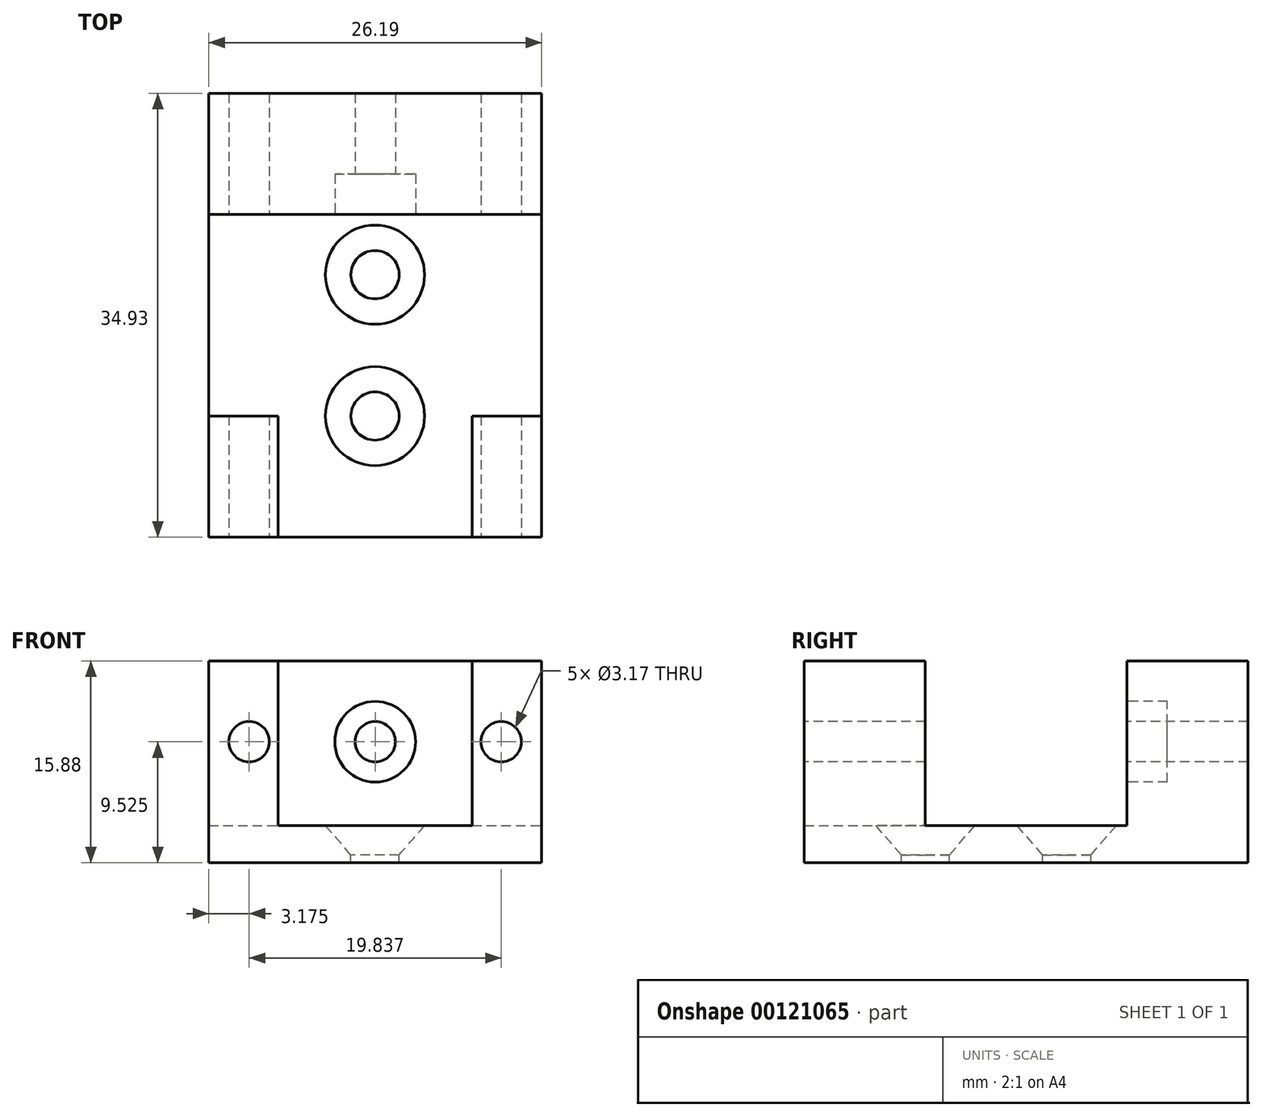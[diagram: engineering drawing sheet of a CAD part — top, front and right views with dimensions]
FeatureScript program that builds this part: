
annotation { "Feature Type Name" : "Feature", "Feature Type Description" : "" }
export const myFeature = defineFeature(function(context is Context, id is Id, definition is map)
    precondition{}
    {
        {
            var Q0;
            Q0=qCreatedBy(makeId("Top.planeOp"),FACE);
            var sketch = newSketch(context, id + "F0", { "sketchPlane" : qUnion([Q0])});
            skLineSegment(sketch, "E0.bottom", {"start": v(0, 0) * mm, "end": v(26.19, 0) * mm});
            skLineSegment(sketch, "E0.top", {"start": v(0, 34.93) * mm, "end": v(26.19, 34.93) * mm});
            skLineSegment(sketch, "E0.left", {"start": v(0, 0) * mm, "end": v(0, 34.93) * mm});
            skLineSegment(sketch, "E0.right", {"start": v(26.19, 0) * mm, "end": v(26.19, 34.93) * mm});
            skSolve(sketch);
        }
        {
            var Q0;
            Q0 = qSketchRegion(id + "F0", true);
            extrude(context, id + "F1", {"entities" : qUnion([Q0]), "depth" : 15.88 * mm});
        }
        {
            var Q0;
            Q0=makeQuery(id+"F1.opExtrude","CAP_FACE",FACE,{"disambiguationData":[OSD([sQuery(id+"F0.wireOp",EDGE,"E0.bottom"),sQuery(id+"F0.wireOp",EDGE,"E0.top"),sQuery(id+"F0.wireOp",EDGE,"E0.left"),sQuery(id+"F0.wireOp",EDGE,"E0.right")])],"isStart":false});
            var sketch = newSketch(context, id + "F2", { "sketchPlane" : qUnion([Q0])});
            skLineSegment(sketch, "E1", {"start": v(0, 25.4) * mm, "end": v(26.19, 25.4) * mm});
            skLineSegment(sketch, "E2", {"start": v(26.19, 25.4) * mm, "end": v(26.19, 9.53) * mm});
            skLineSegment(sketch, "E3", {"start": v(26.19, 9.53) * mm, "end": v(20.73, 9.53) * mm});
            skLineSegment(sketch, "E4", {"start": v(20.73, 9.52) * mm, "end": v(20.73, 0) * mm});
            skLineSegment(sketch, "E5", {"start": v(20.73, 0) * mm, "end": v(5.46, 0) * mm});
            skLineSegment(sketch, "E6", {"start": v(5.46, 0) * mm, "end": v(5.46, 9.53) * mm});
            skLineSegment(sketch, "E7", {"start": v(5.46, 9.53) * mm, "end": v(0, 9.53) * mm});
            skLineSegment(sketch, "E8", {"start": v(0, 9.53) * mm, "end": v(0, 25.4) * mm});
            skSolve(sketch);
        }
        {
            var Q0;
            Q0 = qSketchRegion(id + "F2", true);
            extrude(context, id + "F3", {"entities" : qUnion([Q0]), "operationType" : NewBodyOperationType.REMOVE, "oppositeDirection" : true, "depth" : 12.95 * mm});
        }
        {
            var Q0;
            Q0=makeQuery(id+"F1.opExtrude","SWEPT_FACE",FACE,{"disambiguationData":[OSD([sQuery(id+"F0.wireOp",EDGE,"E0.bottom")])]});
            var sketch = newSketch(context, id + "F4", { "sketchPlane" : qUnion([Q0])});
            skCircle(sketch, "E9", {"center": v(3.18, 9.52) * mm, "radius": 1.59 * mm});
            skCircle(sketch, "E10", {"center": v(23.01, 9.52) * mm, "radius": 1.59 * mm});
            skSolve(sketch);
        }
        {
            var Q0;
            Q0 = qSketchRegion(id + "F4", true);
            extrude(context, id + "F5", {"entities" : qUnion([Q0]), "operationType" : NewBodyOperationType.REMOVE, "endBound" : BoundingType.THROUGH_ALL, "oppositeDirection" : true, "depth" : 25.4 * mm});
        }
        {
            var Q0;
            Q0=makeQuery(id+"F3.boolean.opBoolean","COPY",FACE,{"derivedFrom":makeQuery(id+"F3.opExtrude","SWEPT_FACE",FACE,{"disambiguationData":[OSD([sQuery(id+"F2.wireOp",EDGE,"E1")])]})});
            var sketch = newSketch(context, id + "F6", { "sketchPlane" : qUnion([Q0])});
            skCircle(sketch, "E11", {"center": v(13.1, 9.52) * mm, "radius": 1.59 * mm});
            skSolve(sketch);
        }
        {
            var Q0;
            Q0 = qSketchRegion(id + "F6", true);
            extrude(context, id + "F7", {"entities" : qUnion([Q0]), "operationType" : NewBodyOperationType.REMOVE, "endBound" : BoundingType.THROUGH_ALL, "oppositeDirection" : true, "depth" : 25.4 * mm});
        }
        {
            var Q0;
            Q0=makeQuery(id+"F3.boolean.opBoolean","COPY",FACE,{"derivedFrom":makeQuery(id+"F3.opExtrude","CAP_FACE",FACE,{"disambiguationData":[OSD([sQuery(id+"F2.wireOp",EDGE,"E1"),sQuery(id+"F2.wireOp",EDGE,"E2"),sQuery(id+"F2.wireOp",EDGE,"E3"),sQuery(id+"F2.wireOp",EDGE,"E4"),sQuery(id+"F2.wireOp",EDGE,"E5"),sQuery(id+"F2.wireOp",EDGE,"E6"),sQuery(id+"F2.wireOp",EDGE,"E7"),sQuery(id+"F2.wireOp",EDGE,"E8")])],"isStart":false})});
            var sketch = newSketch(context, id + "F8", { "sketchPlane" : qUnion([Q0])});
            skPoint(sketch, "E12", {"position": v(13.08, 9.53) * mm});
            skPoint(sketch, "E13", {"position": v(13.08, 20.65) * mm});
            skSolve(sketch);
        }
        {
            var Q0;
            Q0=sQuery(id+"F8.wireOp",VERTEX,"E13");
            var Q1;
            Q1=sQuery(id+"F8.wireOp",VERTEX,"E12");
            var Q2;
            Q2=makeQuery(id+"F1.opExtrude","SWEPT_BODY",BODY,{"disambiguationData":[OSD([sQuery(id+"F0.wireOp",EDGE,"E0.bottom"),sQuery(id+"F0.wireOp",EDGE,"E0.top"),sQuery(id+"F0.wireOp",EDGE,"E0.left"),sQuery(id+"F0.wireOp",EDGE,"E0.right")])]});
            hole(context, id + "F9", {"style" : HoleStyle.C_SINK, "endStyle" : HoleEndStyle.THROUGH, "standardTappedOrClearance" : lookupTablePath({ "standard" : "ANSI", "fit" : "Normal (ASME)", "size" : "#6", "type" : "Clearance" }), "standardBlindInLast" : lookupTablePath({ "fit" : "Free", "standard" : "ANSI", "size" : "#6", "type" : "Clearance" }), "holeDiameter" : 3.8 * mm, "cSinkDiameter" : 7.8 * mm, "cSinkAngle" : 82 * degree, "startFromSketch" : true, "locations" : qUnion([Q0, Q1]), "scope" : qUnion([Q2]), "isTappedThrough" : true});
        }
        {
            var Q0;
            Q0=makeQuery(id+"F3.boolean.opBoolean","COPY",FACE,{"derivedFrom":makeQuery(id+"F3.opExtrude","SWEPT_FACE",FACE,{"disambiguationData":[OSD([sQuery(id+"F2.wireOp",EDGE,"E1")])]})});
            var sketch = newSketch(context, id + "F10", { "sketchPlane" : qUnion([Q0])});
            skCircle(sketch, "E14", {"center": v(13.1, 9.53) * mm, "radius": 3.18 * mm});
            skSolve(sketch);
        }
        {
            var Q0;
            Q0=makeQuery(id+"F10.imprint","IMPRINT",FACE,{"disambiguationData":[TD([[makeQuery(id+"F10.imprint","IMPRINT",EDGE,{"derivedFrom":sQuery(id+"F10.wireOp",EDGE,"E14")}),1.0]])]});
            extrude(context, id + "F11", {"entities" : qUnion([Q0]), "operationType" : NewBodyOperationType.REMOVE, "oppositeDirection" : true, "depth" : 3.17 * mm});
        }
    });
